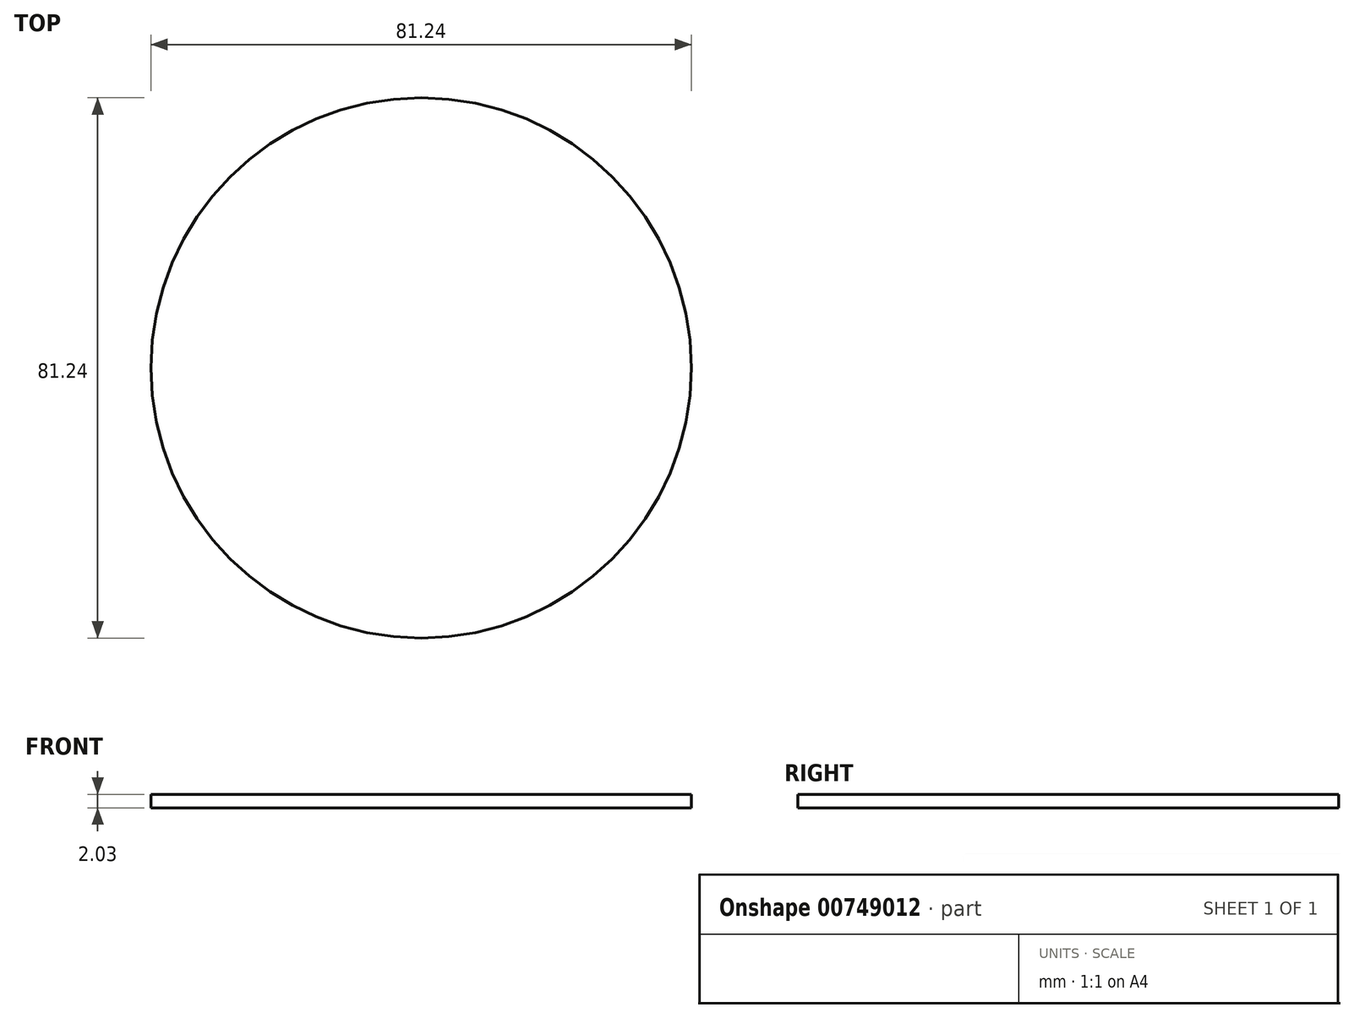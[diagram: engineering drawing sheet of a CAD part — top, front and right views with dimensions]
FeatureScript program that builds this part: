
annotation { "Feature Type Name" : "Feature", "Feature Type Description" : "" }
export const myFeature = defineFeature(function(context is Context, id is Id, definition is map)
    precondition{}
    {
        {
            var Q0;
            Q0=qCreatedBy(makeId("Top.planeOp"),FACE);
            var sketch = newSketch(context, id + "F0", { "sketchPlane" : qUnion([Q0])});
            skCircle(sketch, "E0", {"center": v(0, 0) * mm, "radius": 40.62 * mm});
            skSolve(sketch);
        }
        {
            var Q0;
            Q0 = qSketchRegion(id + "F0", true);
            extrude(context, id + "F1", {"entities" : qUnion([Q0]), "depth" : 2.03 * mm, "offsetDistance" : 25.4 * mm});
        }
    });
